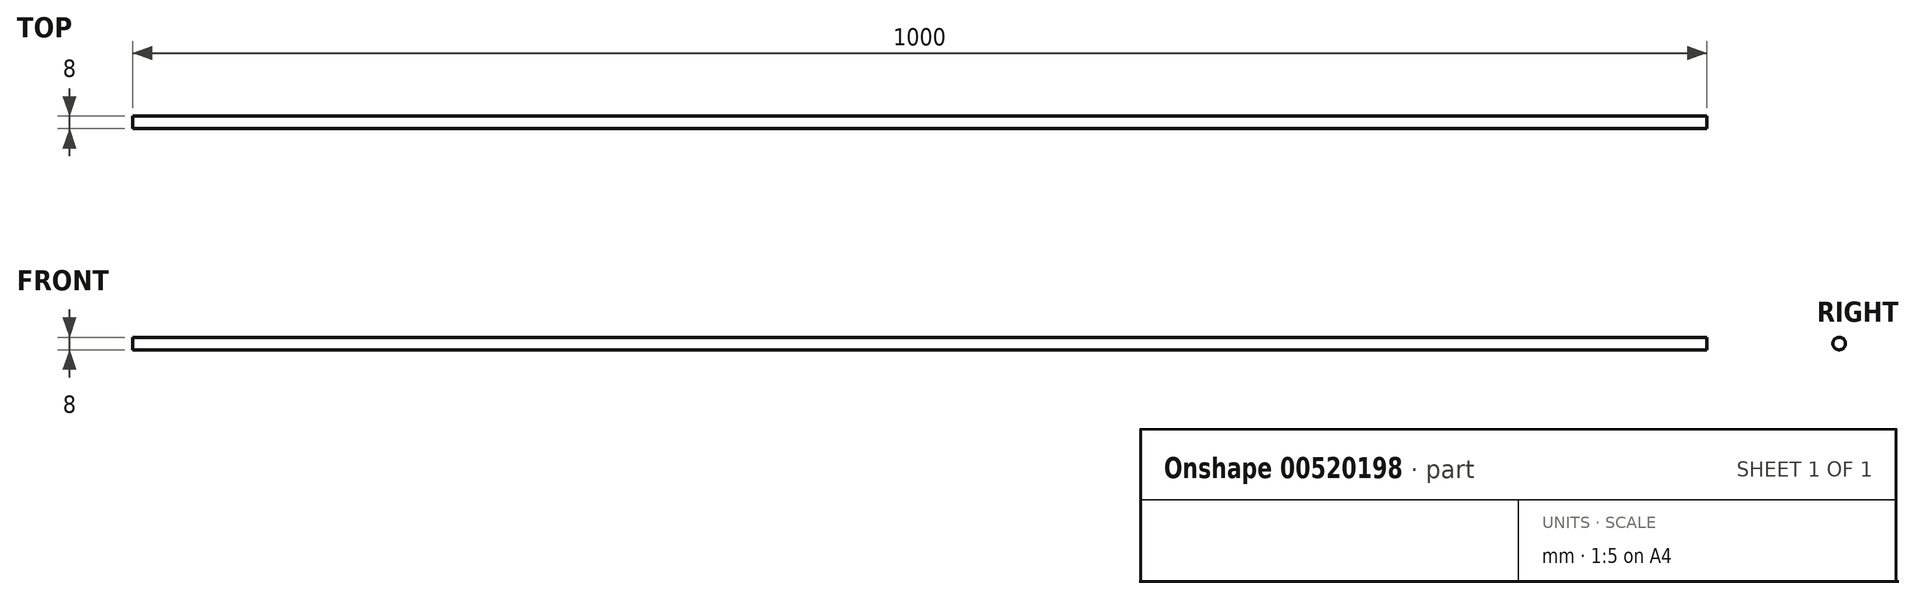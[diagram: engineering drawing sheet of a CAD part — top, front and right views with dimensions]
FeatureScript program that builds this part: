
annotation { "Feature Type Name" : "Feature", "Feature Type Description" : "" }
export const myFeature = defineFeature(function(context is Context, id is Id, definition is map)
    precondition{}
    {
        {
            var Q0;
            Q0=qCreatedBy(makeId("Right.planeOp"),FACE);
            var sketch = newSketch(context, id + "F0", { "sketchPlane" : qUnion([Q0])});
            skCircle(sketch, "E0", {"center": v(0, 0) * mm, "radius": 4 * mm});
            skSolve(sketch);
        }
        {
            var Q0;
            Q0 = qSketchRegion(id + "F0", true);
            extrude(context, id + "F1", {"entities" : qUnion([Q0]), "endBound" : BoundingType.SYMMETRIC, "depth" : 1000 * mm, "offsetDistance" : 25 * mm});
        }
    });
